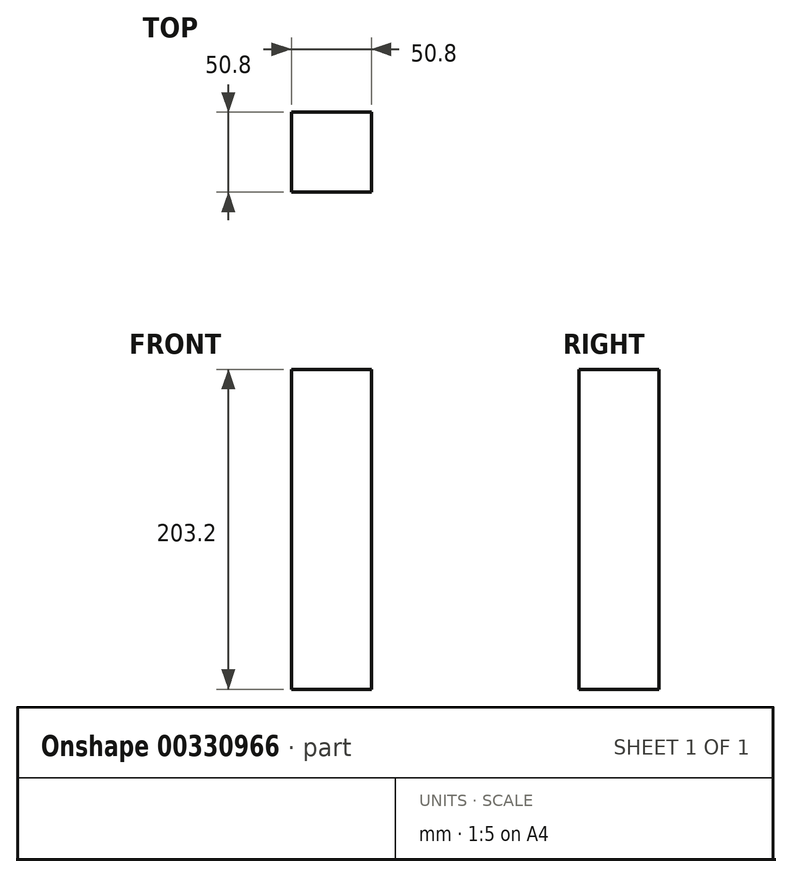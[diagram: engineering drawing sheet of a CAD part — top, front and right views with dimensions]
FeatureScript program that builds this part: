
annotation { "Feature Type Name" : "Feature", "Feature Type Description" : "" }
export const myFeature = defineFeature(function(context is Context, id is Id, definition is map)
    precondition{}
    {
        {
            var Q0;
            Q0=qCreatedBy(makeId("Top.planeOp"),FACE);
            var sketch = newSketch(context, id + "F0", { "sketchPlane" : qUnion([Q0])});
            skLineSegment(sketch, "E0.bottom", {"start": v(0, 0) * mm, "end": v(50.8, 0) * mm});
            skLineSegment(sketch, "E0.top", {"start": v(0, 50.8) * mm, "end": v(50.8, 50.8) * mm});
            skLineSegment(sketch, "E0.left", {"start": v(0, 0) * mm, "end": v(0, 50.8) * mm});
            skLineSegment(sketch, "E0.right", {"start": v(50.8, 0) * mm, "end": v(50.8, 50.8) * mm});
            skSolve(sketch);
        }
        {
            var Q0;
            Q0 = qSketchRegion(id + "F0", true);
            extrude(context, id + "F1", {"entities" : qUnion([Q0]), "depth" : 203.2 * mm});
        }
    });
